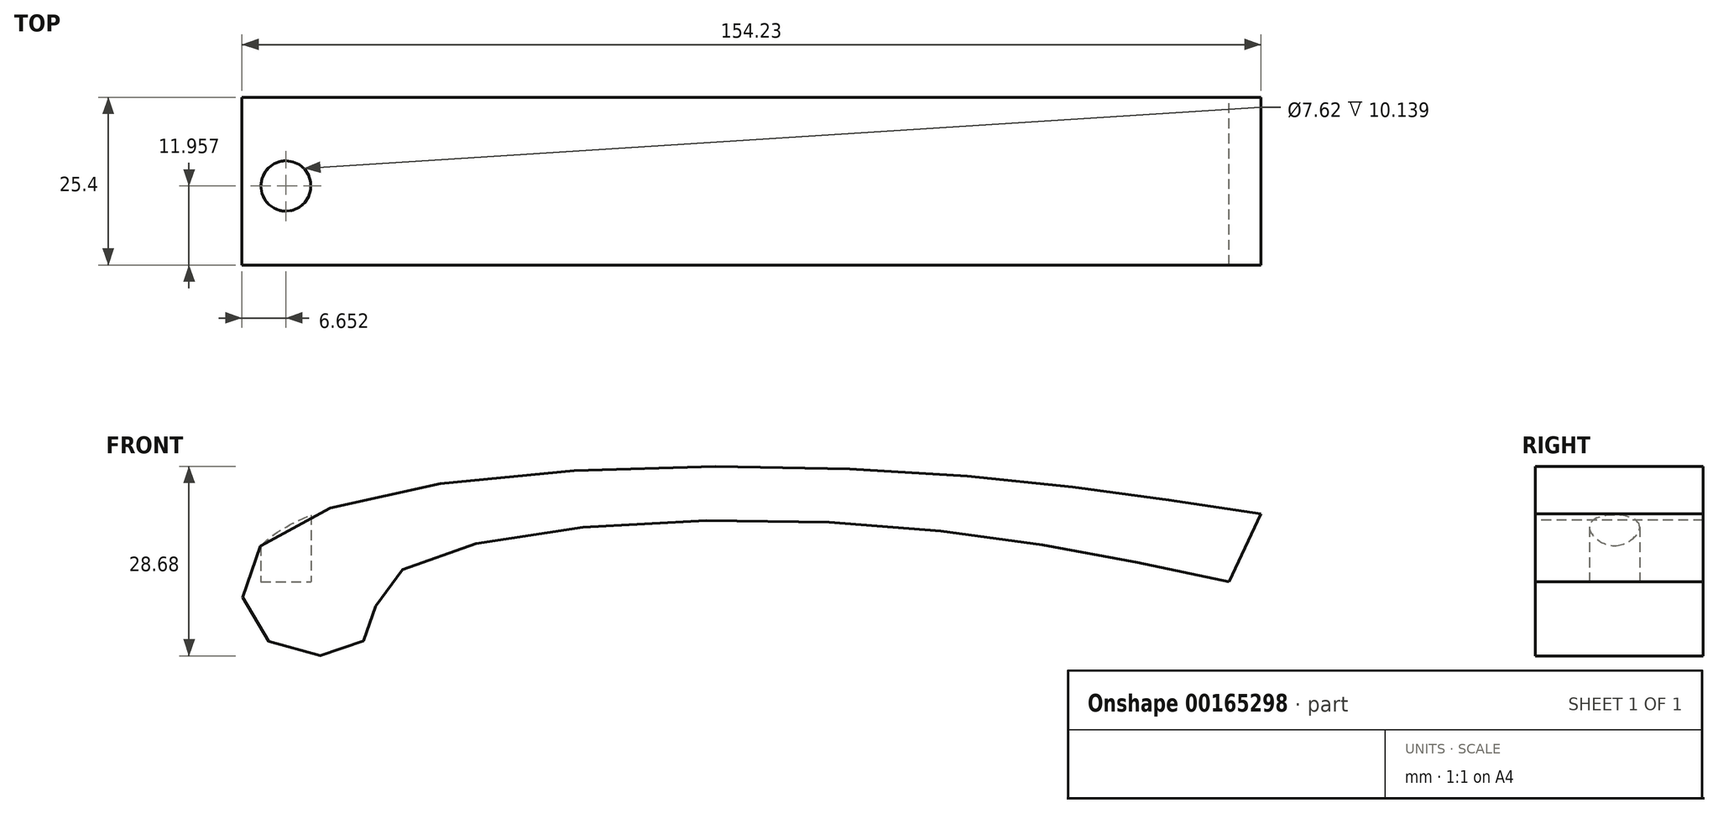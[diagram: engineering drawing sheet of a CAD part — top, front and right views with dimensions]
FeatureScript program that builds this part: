
annotation { "Feature Type Name" : "Feature", "Feature Type Description" : "" }
export const myFeature = defineFeature(function(context is Context, id is Id, definition is map)
    precondition{}
    {
        {
            var Q0;
            Q0=qCreatedBy(makeId("Front.planeOp"),FACE);
            var sketch = newSketch(context, id + "F0", { "sketchPlane" : qUnion([Q0])});
            skFitSpline(sketch, "E0", {"points": [v(63.97, 0) * mm, v(0, 9.18) * mm, v(-63.41, 0) * mm, v(-66.94, -8.8) * mm, v(-80.84, -9.36) * mm, v(-83.44, 4.54) * mm, v(0, 17.34) * mm, v(68.8, 10.3) * mm], "startDerivative": vector(-317.35, 68.64) * mm, "endDerivative": vector(318.41, -50) * mm});
            skLineSegment(sketch, "E1", {"start": v(63.97, 0) * mm, "end": v(68.8, 10.3) * mm});
            skSolve(sketch);
        }
        {
            var Q0;
            Q0 = qSketchRegion(id + "F0", true);
            var Q1;
            Q1=makeQuery(id+"F0.imprint","IMPRINT",FACE,{"disambiguationData":[TD([[makeQuery(id+"F0.imprint","IMPRINT",EDGE,{"derivedFrom":sQuery(id+"F0.wireOp",EDGE,"E0")}),-1.0]])]});
            extrude(context, id + "F1", {"entities" : qUnion([Q0, Q1]), "depth" : 25.4 * mm});
        }
        {
            var Q0;
            Q0=qCreatedBy(makeId("Top.planeOp"),FACE);
            var sketch = newSketch(context, id + "F2", { "sketchPlane" : qUnion([Q0])});
            skPoint(sketch, "E2", {"position": v(-78.79, -13.44) * mm});
            skSolve(sketch);
        }
        {
            var Q0;
            Q0=sQuery(id+"F2.wireOp",VERTEX,"E2");
            var Q1;
            Q1=makeQuery(id+"F1.opExtrude","SWEPT_BODY",BODY,{"disambiguationData":[OSD([sQuery(id+"F0.wireOp",EDGE,"E0"),sQuery(id+"F0.wireOp",EDGE,"E1")])]});
            hole(context, id + "F3", {"style" : HoleStyle.SIMPLE, "endStyle" : HoleEndStyle.THROUGH, "oppositeDirection" : true, "holeDiameter" : 7.62 * mm, "locations" : qUnion([Q0]), "scope" : qUnion([Q1]), "isTappedThrough" : true});
        }
    });
